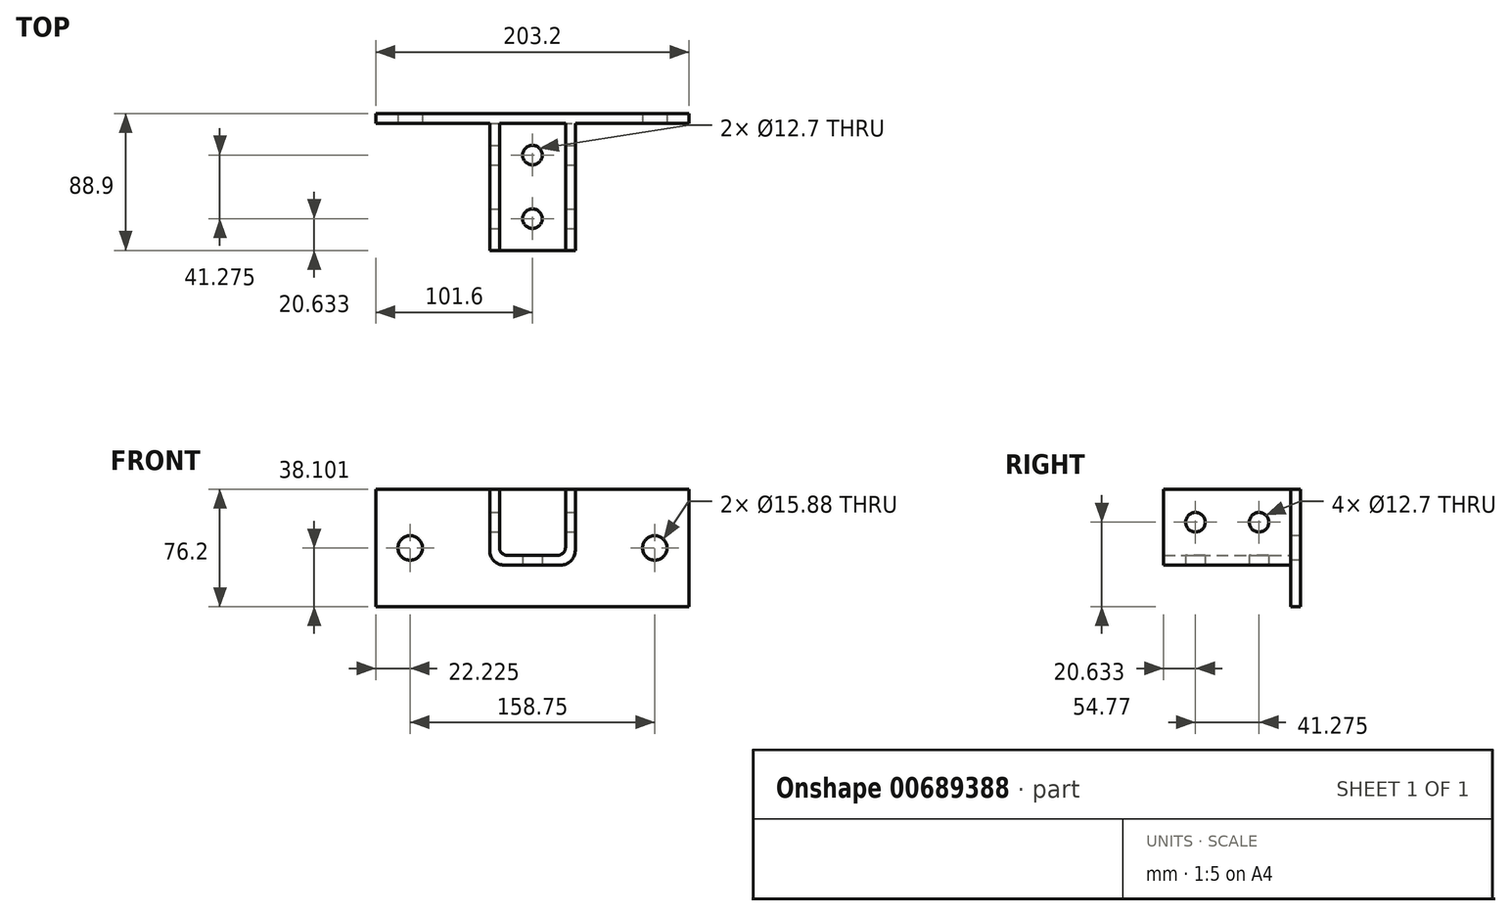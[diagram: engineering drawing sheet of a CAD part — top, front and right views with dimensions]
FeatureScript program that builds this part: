
annotation { "Feature Type Name" : "Feature", "Feature Type Description" : "" }
export const myFeature = defineFeature(function(context is Context, id is Id, definition is map)
    precondition{}
    {
        {
            var Q0;
            Q0=qCreatedBy(makeId("Front.planeOp"),FACE);
            var sketch = newSketch(context, id + "F0", { "sketchPlane" : qUnion([Q0])});
            skLineSegment(sketch, "E0.bottom", {"start": v(21.43, -21.43) * mm, "end": v(-21.43, -21.43) * mm});
            skLineSegment(sketch, "E0.left", {"start": v(21.43, -21.43) * mm, "end": v(21.43, 21.43) * mm});
            skLineSegment(sketch, "E0.right", {"start": v(-21.43, -21.43) * mm, "end": v(-21.43, 21.43) * mm});
            skPoint(sketch, "E0.middle", {"position": v(0, 0) * mm});
            skLineSegment(sketch, "E1.0", {"start": v(27.78, -21.43) * mm, "end": v(27.78, 21.43) * mm});
            skLineSegment(sketch, "E2.0", {"start": v(21.43, -27.78) * mm, "end": v(-21.43, -27.78) * mm});
            skLineSegment(sketch, "E3.0", {"start": v(-27.78, -21.43) * mm, "end": v(-27.78, 21.43) * mm});
            skLineSegment(sketch, "E4", {"start": v(-27.78, -21.43) * mm, "end": v(-27.78, -27.78) * mm});
            skLineSegment(sketch, "E5", {"start": v(-27.78, -27.78) * mm, "end": v(-21.43, -27.78) * mm});
            skLineSegment(sketch, "E6", {"start": v(27.78, -21.43) * mm, "end": v(27.78, -27.78) * mm});
            skLineSegment(sketch, "E7", {"start": v(27.78, -27.78) * mm, "end": v(21.43, -27.78) * mm});
            skLineSegment(sketch, "E8", {"start": v(27.78, 21.43) * mm, "end": v(21.43, 21.43) * mm});
            skLineSegment(sketch, "E9", {"start": v(-21.43, 21.43) * mm, "end": v(-27.78, 21.43) * mm});
            skSolve(sketch);
        }
        {
            var Q0;
            Q0 = qSketchRegion(id + "F0", true);
            extrude(context, id + "F1", {"entities" : qUnion([Q0]), "depth" : 82.55 * mm, "offsetDistance" : 25.4 * mm, "symmetric" : true});
        }
        {
            var Q0;
            Q0=makeQuery(id+"F1.opExtrude","SWEPT_EDGE",EDGE,{"disambiguationData":[OSD([sQuery(id+"F0.wireOp",EDGE,"E0.bottom"),sQuery(id+"F0.wireOp",EDGE,"E0.right")])]});
            var Q1;
            Q1=makeQuery(id+"F1.opExtrude","SWEPT_EDGE",EDGE,{"disambiguationData":[OSD([sQuery(id+"F0.wireOp",EDGE,"E0.bottom"),sQuery(id+"F0.wireOp",EDGE,"E0.left")])]});
            fillet(context, id + "F2", {"entities" : qUnion([Q0, Q1]), "radius" : 5.08 * mm, "tangentPropagation" : true, "allowEdgeOverflow" : false});
        }
        {
            var Q0;
            Q0=makeQuery(id+"F1.opExtrude","SWEPT_EDGE",EDGE,{"disambiguationData":[OSD([sQuery(id+"F0.wireOp",EDGE,"E4"),sQuery(id+"F0.wireOp",EDGE,"E5")])]});
            var Q1;
            Q1=makeQuery(id+"F1.opExtrude","SWEPT_EDGE",EDGE,{"disambiguationData":[OSD([sQuery(id+"F0.wireOp",EDGE,"E6"),sQuery(id+"F0.wireOp",EDGE,"E7")])]});
            fillet(context, id + "F3", {"entities" : qUnion([Q0, Q1]), "radius" : 9.52 * mm, "tangentPropagation" : true, "allowEdgeOverflow" : false});
        }
        {
            var Q0;
            Q0=makeQuery(id+"F1.opExtrude","SWEPT_FACE",FACE,{"disambiguationData":[OSD([sQuery(id+"F0.wireOp",EDGE,"E1.0"),sQuery(id+"F0.wireOp",EDGE,"E6")])]});
            var sketch = newSketch(context, id + "F4", { "sketchPlane" : qUnion([Q0])});
            skCircle(sketch, "E10", {"center": v(-20.64, 0) * mm, "radius": 6.35 * mm});
            skCircle(sketch, "E11.MirrorC", {"center": v(20.64, 0) * mm, "radius": 6.35 * mm});
            skSolve(sketch);
        }
        {
            var Q0;
            Q0 = qSketchRegion(id + "F4", true);
            extrude(context, id + "F5", {"entities" : qUnion([Q0]), "operationType" : NewBodyOperationType.REMOVE, "endBound" : BoundingType.THROUGH_ALL, "oppositeDirection" : true, "depth" : 25.4 * mm, "offsetDistance" : 25.4 * mm});
        }
        {
            var Q0;
            Q0=makeQuery(id+"F1.opExtrude","SWEPT_FACE",FACE,{"disambiguationData":[OSD([sQuery(id+"F0.wireOp",EDGE,"E2.0"),sQuery(id+"F0.wireOp",EDGE,"E5"),sQuery(id+"F0.wireOp",EDGE,"E7")])]});
            var sketch = newSketch(context, id + "F6", { "sketchPlane" : qUnion([Q0])});
            skCircle(sketch, "E12", {"center": v(0, 20.64) * mm, "radius": 6.35 * mm});
            skCircle(sketch, "E13.MirrorC", {"center": v(0, -20.64) * mm, "radius": 6.35 * mm});
            skSolve(sketch);
        }
        {
            var Q0;
            Q0 = qSketchRegion(id + "F6", true);
            extrude(context, id + "F7", {"entities" : qUnion([Q0]), "operationType" : NewBodyOperationType.REMOVE, "oppositeDirection" : true, "depth" : 25.4 * mm, "offsetDistance" : 25.4 * mm});
        }
        {
            var Q0;
            Q0=makeQuery(id+"F1.opExtrude","CAP_FACE",FACE,{"disambiguationData":[OSD([sQuery(id+"F0.wireOp",EDGE,"E0.bottom"),sQuery(id+"F0.wireOp",EDGE,"E0.left"),sQuery(id+"F0.wireOp",EDGE,"E0.right"),sQuery(id+"F0.wireOp",EDGE,"E1.0"),sQuery(id+"F0.wireOp",EDGE,"E2.0"),sQuery(id+"F0.wireOp",EDGE,"E3.0"),sQuery(id+"F0.wireOp",EDGE,"E4"),sQuery(id+"F0.wireOp",EDGE,"E5"),sQuery(id+"F0.wireOp",EDGE,"E6"),sQuery(id+"F0.wireOp",EDGE,"E7"),sQuery(id+"F0.wireOp",EDGE,"E8"),sQuery(id+"F0.wireOp",EDGE,"E9")])],"isStart":true});
            var sketch = newSketch(context, id + "F8", { "sketchPlane" : qUnion([Q0])});
            skLineSegment(sketch, "E14.bottom", {"start": v(101.6, -54.77) * mm, "end": v(-101.6, -54.77) * mm});
            skLineSegment(sketch, "E14.top", {"start": v(101.6, 21.43) * mm, "end": v(-101.6, 21.43) * mm});
            skLineSegment(sketch, "E14.left", {"start": v(101.6, -54.77) * mm, "end": v(101.6, 21.43) * mm});
            skLineSegment(sketch, "E14.right", {"start": v(-101.6, -54.77) * mm, "end": v(-101.6, 21.43) * mm});
            skPoint(sketch, "E14.middle", {"position": v(0, -16.67) * mm});
            skCircle(sketch, "E15", {"center": v(-79.38, -16.67) * mm, "radius": 7.94 * mm});
            skPoint(sketch, "E15.centerSnap0", {"position": v(-101.6, -16.67) * mm});
            skCircle(sketch, "E16.MirrorC", {"center": v(79.38, -16.67) * mm, "radius": 7.94 * mm});
            skSolve(sketch);
        }
        {
            var Q0;
            Q0 = qSketchRegion(id + "F8", true);
            extrude(context, id + "F9", {"entities" : qUnion([Q0]), "operationType" : NewBodyOperationType.ADD, "depth" : 6.35 * mm, "offsetDistance" : 25.4 * mm});
        }
    });
